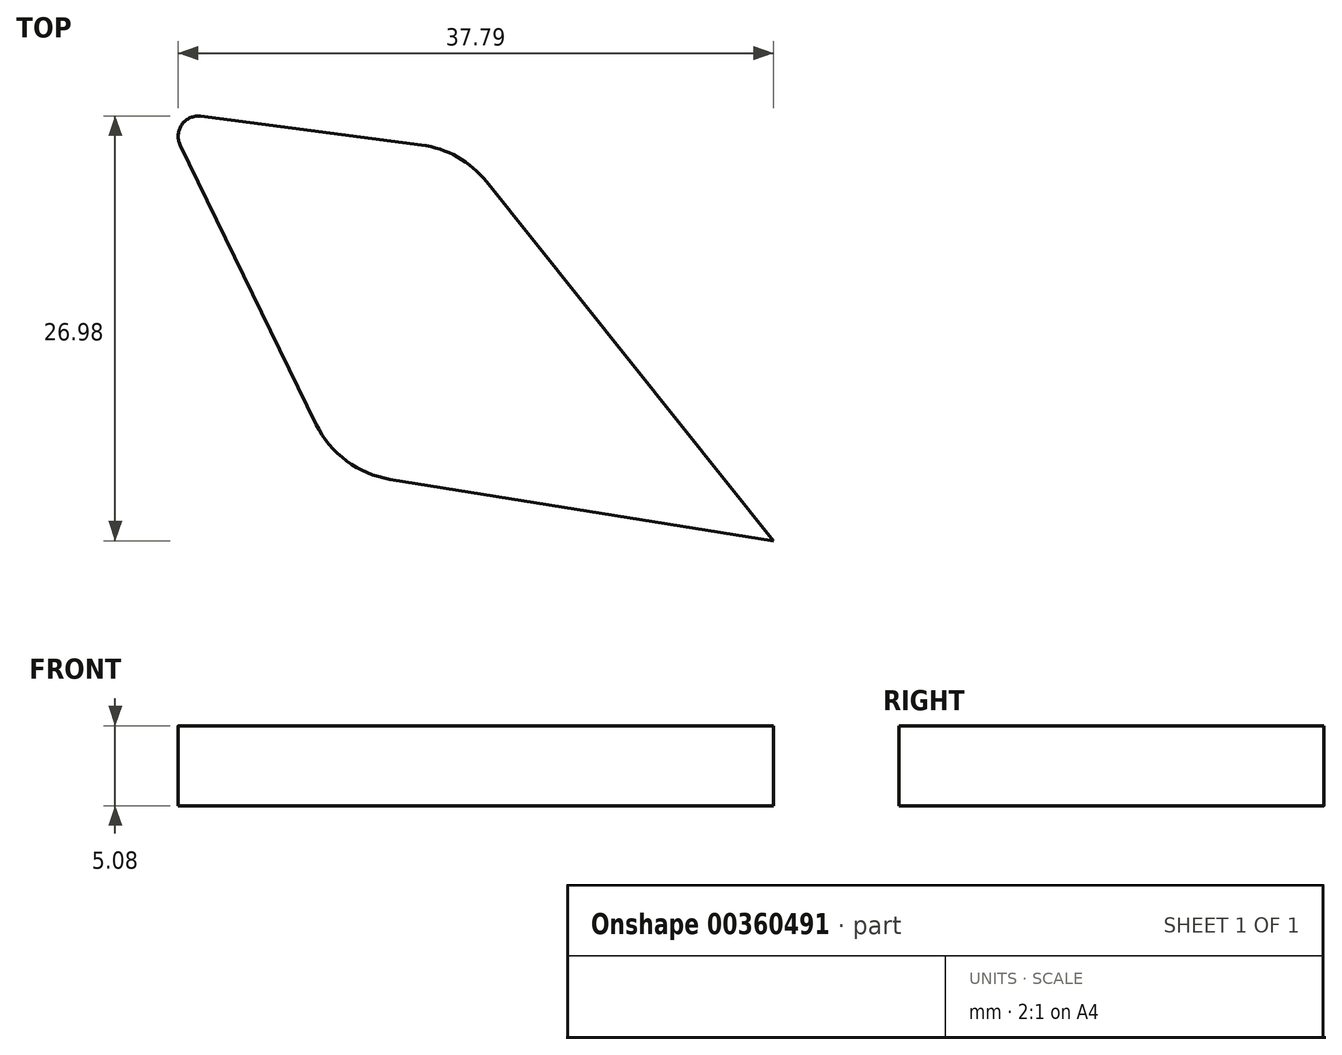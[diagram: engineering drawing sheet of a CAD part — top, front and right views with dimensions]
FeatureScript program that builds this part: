
annotation { "Feature Type Name" : "Feature", "Feature Type Description" : "" }
export const myFeature = defineFeature(function(context is Context, id is Id, definition is map)
    precondition{}
    {
        {
            var Q0;
            Q0=qCreatedBy(makeId("Top.planeOp"),FACE);
            var sketch = newSketch(context, id + "F0", { "sketchPlane" : qUnion([Q0])});
            skLineSegment(sketch, "E0", {"start": v(-26.08, 33.46) * mm, "end": v(-44.28, 56.27) * mm});
            skLineSegment(sketch, "E1", {"start": v(-48.43, 58.6) * mm, "end": v(-62.44, 60.43) * mm});
            skLineSegment(sketch, "E2", {"start": v(-63.74, 58.61) * mm, "end": v(-55.1, 40.86) * mm});
            skLineSegment(sketch, "E3", {"start": v(-50.4, 37.37) * mm, "end": v(-26.08, 33.46) * mm});
            skPoint(sketch, "E4.visualSharp", {"position": v(-45.88, 58.27) * mm});
            skArc(sketch, "E4.filletArc", {"start": v(-44.28, 56.27) * mm, "mid": v(-46.13, 57.84) * mm, "end": v(-48.43, 58.6) * mm});
            skPoint(sketch, "E5.visualSharp", {"position": v(-53.66, 37.9) * mm});
            skArc(sketch, "E5.filletArc", {"start": v(-55.1, 40.86) * mm, "mid": v(-53.18, 38.54) * mm, "end": v(-50.4, 37.37) * mm});
            skPoint(sketch, "E6.visualSharp", {"position": v(-64.77, 60.73) * mm});
            skArc(sketch, "E6.filletArc", {"start": v(-62.44, 60.43) * mm, "mid": v(-63.63, 59.9) * mm, "end": v(-63.74, 58.61) * mm});
            skSolve(sketch);
        }
        {
            var Q0;
            Q0=makeQuery(id+"F0.imprint","IMPRINT",FACE,{"disambiguationData":[TD([[makeQuery(id+"F0.imprint","IMPRINT",EDGE,{"derivedFrom":sQuery(id+"F0.wireOp",EDGE,"E0")}),1.0]])]});
            extrude(context, id + "F1", {"entities" : qUnion([Q0]), "depth" : 5.08 * mm});
        }
    });
